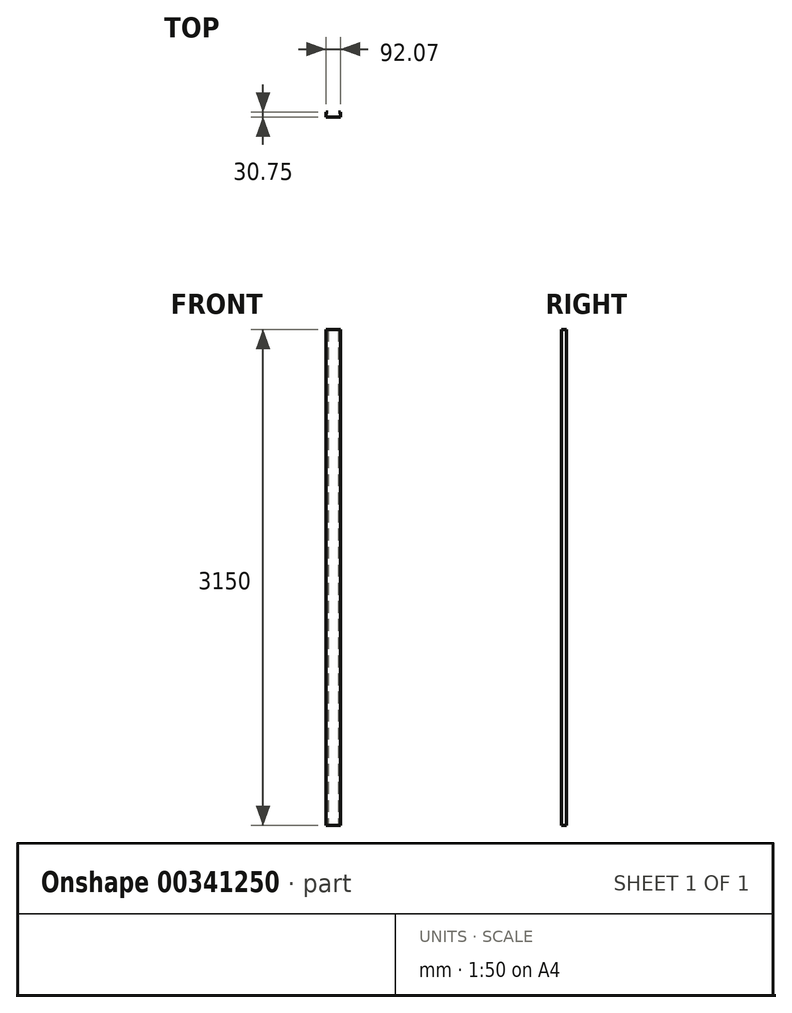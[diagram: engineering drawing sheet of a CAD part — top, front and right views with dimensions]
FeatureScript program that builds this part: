
annotation { "Feature Type Name" : "Feature", "Feature Type Description" : "" }
export const myFeature = defineFeature(function(context is Context, id is Id, definition is map)
    precondition{}
    {
        {
            var Q0;
            Q0=qCreatedBy(makeId("Top.planeOp"),FACE);
            var sketch = newSketch(context, id + "F0", { "sketchPlane" : qUnion([Q0])});
            skLineSegment(sketch, "E0", {"start": v(-91.26, 0) * mm, "end": v(-0.1, 0) * mm});
            skLineSegment(sketch, "E1", {"start": v(-0.1, 0) * mm, "end": v(-0.1, 29.84) * mm});
            skLineSegment(sketch, "E2", {"start": v(-0.1, 29.84) * mm, "end": v(-12.34, 29.84) * mm});
            skLineSegment(sketch, "E3", {"start": v(-91.26, 0) * mm, "end": v(-91.26, 29.84) * mm});
            skLineSegment(sketch, "E4", {"start": v(-91.26, 29.84) * mm, "end": v(-79.01, 29.84) * mm});
            skLineSegment(sketch, "E5.0", {"start": v(-91.71, 30.3) * mm, "end": v(-79.01, 30.3) * mm});
            skLineSegment(sketch, "E5.1", {"start": v(0.36, 30.3) * mm, "end": v(-12.34, 30.3) * mm});
            skLineSegment(sketch, "E5.2", {"start": v(0.36, -0.45) * mm, "end": v(0.36, 30.3) * mm});
            skLineSegment(sketch, "E5.3", {"start": v(-91.71, -0.45) * mm, "end": v(0.36, -0.45) * mm});
            skLineSegment(sketch, "E5.4", {"start": v(-91.71, -0.45) * mm, "end": v(-91.71, 30.3) * mm});
            skLineSegment(sketch, "E6", {"start": v(-79.01, 29.84) * mm, "end": v(-79.01, 30.3) * mm});
            skLineSegment(sketch, "E7", {"start": v(-12.34, 29.84) * mm, "end": v(-12.34, 30.3) * mm});
            skSolve(sketch);
        }
        {
            var Q0;
            Q0=makeQuery(id+"F0.imprint","IMPRINT",FACE,{"disambiguationData":[TD([[makeQuery(id+"F0.imprint","IMPRINT",EDGE,{"derivedFrom":sQuery(id+"F0.wireOp",EDGE,"E0")}),-1.0]])]});
            extrude(context, id + "F1", {"entities" : qUnion([Q0]), "depth" : 3150 * mm});
        }
    });
